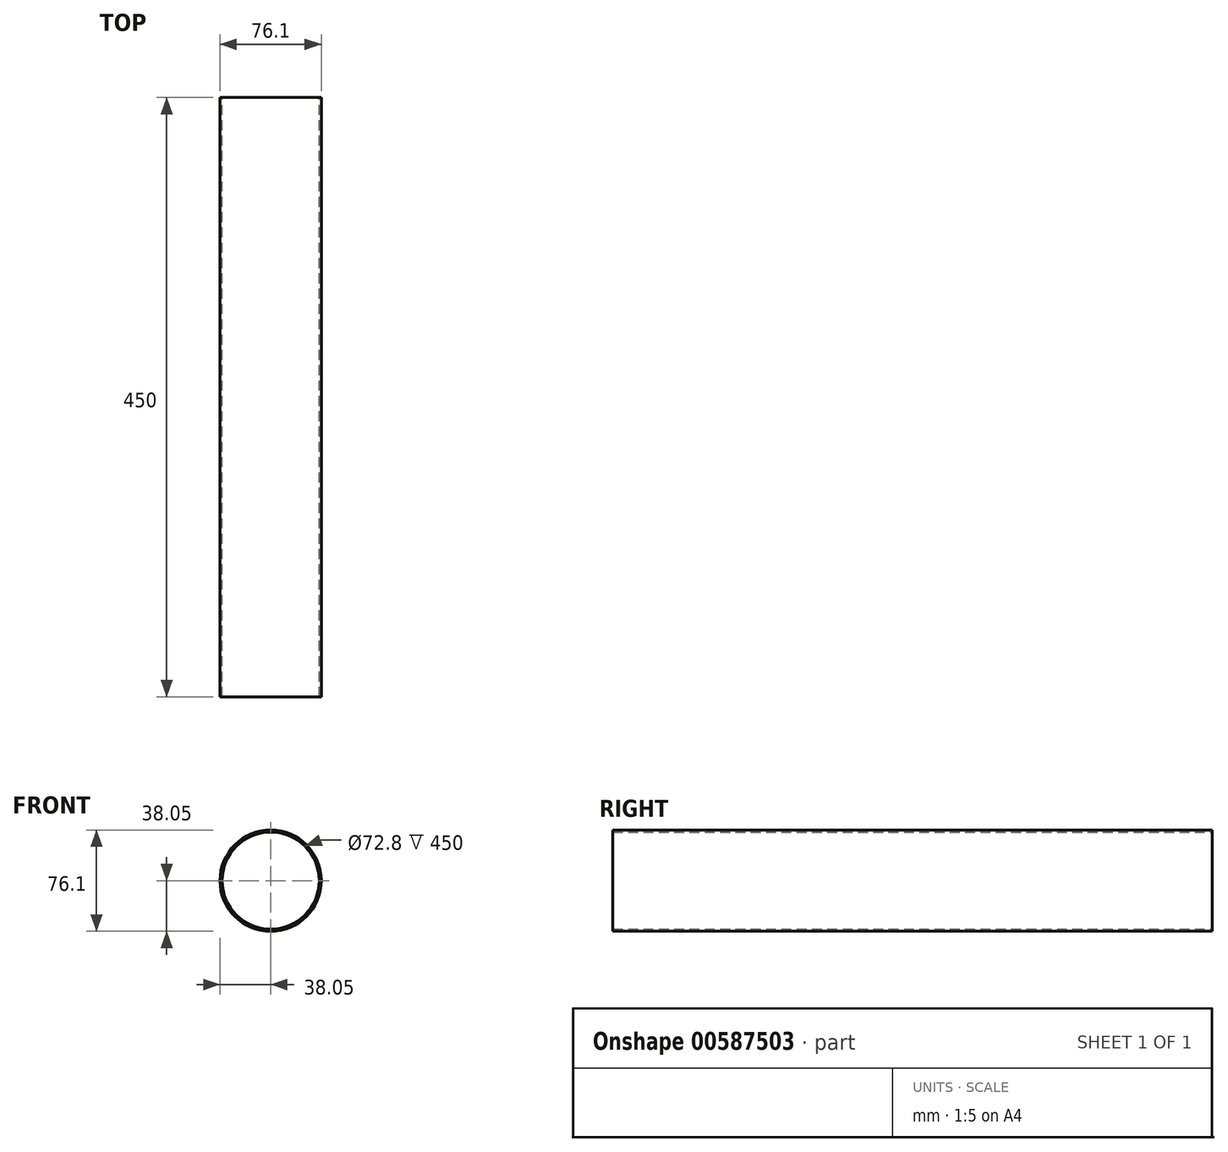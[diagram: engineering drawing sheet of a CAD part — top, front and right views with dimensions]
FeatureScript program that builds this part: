
annotation { "Feature Type Name" : "Feature", "Feature Type Description" : "" }
export const myFeature = defineFeature(function(context is Context, id is Id, definition is map)
    precondition{}
    {
        {
            var Q0;
            Q0=qCreatedBy(makeId("Front.planeOp"),FACE);
            var sketch = newSketch(context, id + "F0", { "sketchPlane" : qUnion([Q0])});
            skCircle(sketch, "E0", {"center": v(0, 0) * mm, "radius": 38.05 * mm});
            skCircle(sketch, "E1.0", {"center": v(0, 0) * mm, "radius": 36.4 * mm});
            skSolve(sketch);
        }
        {
            var Q0;
            Q0=makeQuery(id+"F0.imprint","IMPRINT",FACE,{"disambiguationData":[TD([[makeQuery(id+"F0.imprint","IMPRINT",EDGE,{"derivedFrom":sQuery(id+"F0.wireOp",EDGE,"E0")}),1.0]])]});
            extrude(context, id + "F1", {"entities" : qUnion([Q0]), "depth" : 450 * mm, "offsetDistance" : 25 * mm});
        }
    });
